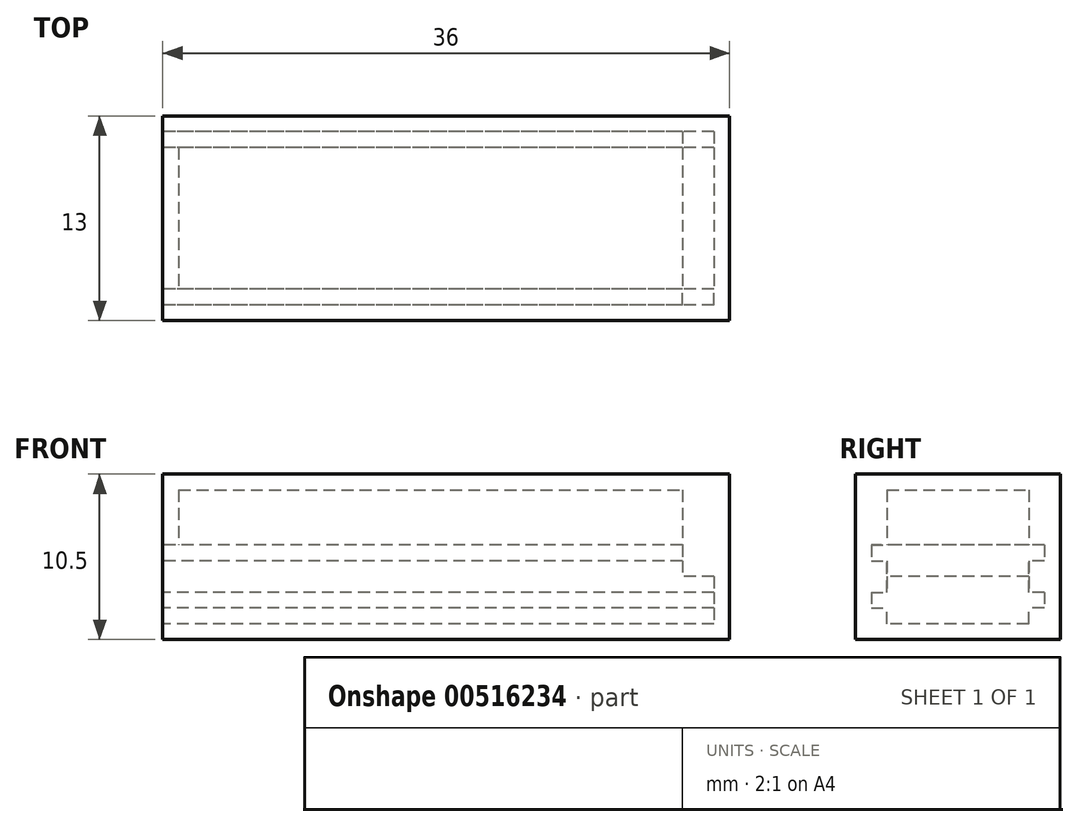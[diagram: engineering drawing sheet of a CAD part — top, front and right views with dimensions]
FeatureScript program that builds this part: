
annotation { "Feature Type Name" : "Feature", "Feature Type Description" : "" }
export const myFeature = defineFeature(function(context is Context, id is Id, definition is map)
    precondition{}
    {
        {
            var Q0;
            Q0=qCreatedBy(makeId("Top.planeOp"),FACE);
            var sketch = newSketch(context, id + "F0", { "sketchPlane" : qUnion([Q0])});
            skLineSegment(sketch, "E0.bottom", {"start": v(-27.77, -4.5) * mm, "end": v(4.23, -4.5) * mm});
            skLineSegment(sketch, "E0.top", {"start": v(-27.77, 4.5) * mm, "end": v(4.23, 4.5) * mm});
            skLineSegment(sketch, "E0.left", {"start": v(-27.77, -4.5) * mm, "end": v(-27.77, 4.5) * mm});
            skLineSegment(sketch, "E0.right", {"start": v(4.23, -4.5) * mm, "end": v(4.23, 4.5) * mm});
            skLineSegment(sketch, "E1.bottom", {"start": v(-28.77, -6.5) * mm, "end": v(7.23, -6.5) * mm});
            skLineSegment(sketch, "E1.top", {"start": v(-28.77, 6.5) * mm, "end": v(7.23, 6.5) * mm});
            skLineSegment(sketch, "E1.left", {"start": v(-28.77, -6.5) * mm, "end": v(-28.77, 6.5) * mm});
            skLineSegment(sketch, "E1.right", {"start": v(7.23, -6.5) * mm, "end": v(7.23, 6.5) * mm});
            skLineSegment(sketch, "E2", {"start": v(-28.77, 0) * mm, "end": v(7.23, 0) * mm, "construction": true});
            skLineSegment(sketch, "E3", {"start": v(-27.77, -4.5) * mm, "end": v(-28.77, -4.5) * mm});
            skLineSegment(sketch, "E4", {"start": v(-27.77, 4.5) * mm, "end": v(-28.77, 4.5) * mm});
            skSolve(sketch);
        }
        {
            var Q0;
            Q0=makeQuery(id+"F0.imprint","IMPRINT",FACE,{"disambiguationData":[TD([[makeQuery(id+"F0.imprint","IMPRINT",EDGE,{"derivedFrom":sQuery(id+"F0.wireOp",EDGE,"E0.bottom")}),-1.0]])]});
            var Q1;
            Q1=makeQuery(id+"F0.imprint","IMPRINT",FACE,{"disambiguationData":[TD([[makeQuery(id+"F0.imprint","IMPRINT",EDGE,{"derivedFrom":sQuery(id+"F0.wireOp",EDGE,"E0.bottom")}),1.0]])]});
            var Q2;
            Q2=makeQuery(id+"F0.imprint","IMPRINT",FACE,{"disambiguationData":[TD([[makeQuery(id+"F0.imprint","IMPRINT",EDGE,{"derivedFrom":sQuery(id+"F0.wireOp",EDGE,"E0.left")}),1.0]])]});
            extrude(context, id + "F1", {"entities" : qUnion([Q0, Q1, Q2]), "depth" : 6.5 * mm, "offsetDistance" : 25 * mm});
        }
        {
            var Q0;
            Q0=makeQuery(id+"F0.imprint","IMPRINT",FACE,{"disambiguationData":[TD([[makeQuery(id+"F0.imprint","IMPRINT",EDGE,{"derivedFrom":sQuery(id+"F0.wireOp",EDGE,"E0.bottom")}),1.0]])]});
            extrude(context, id + "F2", {"entities" : qUnion([Q0]), "operationType" : NewBodyOperationType.REMOVE, "depth" : 5.5 * mm, "offsetDistance" : 25 * mm});
        }
        {
            var Q0;
            Q0=makeQuery(id+"F0.imprint","IMPRINT",FACE,{"disambiguationData":[TD([[makeQuery(id+"F0.imprint","IMPRINT",EDGE,{"derivedFrom":sQuery(id+"F0.wireOp",EDGE,"E0.bottom")}),-1.0]])]});
            extrude(context, id + "F3", {"entities" : qUnion([Q0]), "operationType" : NewBodyOperationType.ADD, "oppositeDirection" : true, "depth" : 4 * mm, "offsetDistance" : 25 * mm});
        }
        {
            var Q0;
            {var subQ0=sQuery(id+"F0.wireOp",EDGE,"E1.left");Q0=makeQuery(id+"F3.boolean.opBoolean","MERGE",FACE,{"derivedFrom":[makeQuery(id+"F1.opExtrude","SWEPT_FACE",FACE,{"disambiguationData":[OSD([subQ0])]}),makeQuery(id+"F3.opExtrude","SWEPT_FACE",FACE,{"disambiguationData":[OSD([subQ0]),TDD([makeQuery(id+"F0.imprint","IMPRINT",EDGE,{"disambiguationData":[TD([[makeQuery(id+"F0.imprint","INTERSECT",VERTEX,{"derivedFrom":[sQuery(id+"F0.wireOp",EDGE,"E1.bottom"),subQ0]}),-1.0]])],"derivedFrom":subQ0})])]}),makeQuery(id+"F3.opExtrude","SWEPT_FACE",FACE,{"disambiguationData":[OSD([subQ0]),TDD([makeQuery(id+"F0.imprint","IMPRINT",EDGE,{"disambiguationData":[TD([[makeQuery(id+"F0.imprint","INTERSECT",VERTEX,{"derivedFrom":[sQuery(id+"F0.wireOp",EDGE,"E1.top"),subQ0]}),1.0]])],"derivedFrom":subQ0})])]})]});}
            var sketch = newSketch(context, id + "F4", { "sketchPlane" : qUnion([Q0])});
            skLineSegment(sketch, "E5.bottom", {"start": v(-5.5, -1) * mm, "end": v(-4.5, -1) * mm});
            skLineSegment(sketch, "E5.top", {"start": v(-5.5, -2) * mm, "end": v(-4.5, -2) * mm});
            skLineSegment(sketch, "E5.left", {"start": v(-5.5, -1) * mm, "end": v(-5.5, -2) * mm});
            skLineSegment(sketch, "E5.right", {"start": v(-4.5, -1) * mm, "end": v(-4.5, -2) * mm});
            skLineSegment(sketch, "E6", {"start": v(0, 0) * mm, "end": v(0, -9.1) * mm, "construction": true});
            skPoint(sketch, "E6.endSnap0", {"position": v(0, 0) * mm});
            skLineSegment(sketch, "E7.bottom", {"start": v(-4.5, -3) * mm, "end": v(4.5, -3) * mm});
            skLineSegment(sketch, "E7.top", {"start": v(-4.5, -4) * mm, "end": v(4.5, -4) * mm});
            skLineSegment(sketch, "E7.left", {"start": v(-4.5, -3) * mm, "end": v(-4.5, -4) * mm});
            skLineSegment(sketch, "E7.right", {"start": v(4.5, -3) * mm, "end": v(4.5, -4) * mm});
            skLineSegment(sketch, "E8.bottom", {"start": v(-5.5, 2) * mm, "end": v(-4.5, 2) * mm});
            skLineSegment(sketch, "E8.top", {"start": v(-5.5, 1) * mm, "end": v(-4.5, 1) * mm});
            skLineSegment(sketch, "E8.left", {"start": v(-5.5, 2) * mm, "end": v(-5.5, 1) * mm});
            skLineSegment(sketch, "E8.right", {"start": v(-4.5, 2) * mm, "end": v(-4.5, 1) * mm});
            skLineSegment(sketch, "E9.bottom", {"start": v(-4.5, 2) * mm, "end": v(0, 2) * mm});
            skLineSegment(sketch, "E9.top", {"start": v(-4.5, 0) * mm, "end": v(0, 0) * mm});
            skLineSegment(sketch, "E9.left", {"start": v(-4.5, 2) * mm, "end": v(-4.5, 0) * mm});
            skLineSegment(sketch, "E9.right", {"start": v(0, 2) * mm, "end": v(0, 0) * mm});
            skSolve(sketch);
        }
        {
            var Q0;
            Q0=makeQuery(id+"F4.imprint","IMPRINT",FACE,{"disambiguationData":[TD([[makeQuery(id+"F4.imprint","IMPRINT",EDGE,{"derivedFrom":sQuery(id+"F4.wireOp",EDGE,"E5.bottom")}),-1.0]])]});
            extrude(context, id + "F5", {"entities" : qUnion([Q0]), "operationType" : NewBodyOperationType.REMOVE, "oppositeDirection" : true, "depth" : 35 * mm, "offsetDistance" : 25 * mm});
        }
        {
            var Q0;
            Q0=makeQuery(id+"F4.imprint","IMPRINT",FACE,{"disambiguationData":[TD([[makeQuery(id+"F4.imprint","IMPRINT",EDGE,{"derivedFrom":sQuery(id+"F4.wireOp",EDGE,"E8.bottom")}),-1.0]])]});
            var Q1;
            {var subQ3=sQuery(id+"F4.wireOp",EDGE,"E9.bottom");Q1=makeQuery(id+"F4.imprint","IMPRINT",FACE,{"disambiguationData":[TD([[makeQuery(id+"F4.imprint","IMPRINT",EDGE,{"derivedFrom":subQ3}),-1.0]])]});}
            extrude(context, id + "F6", {"entities" : qUnion([Q0, Q1]), "operationType" : NewBodyOperationType.REMOVE, "oppositeDirection" : true, "depth" : 33 * mm, "offsetDistance" : 25 * mm});
        }
        {
            var Q0;
            Q0=makeQuery(id+"F1.opExtrude","SWEPT_BODY",BODY,{"disambiguationData":[OSD([sQuery(id+"F0.wireOp",EDGE,"E1.bottom"),sQuery(id+"F0.wireOp",EDGE,"E1.top"),sQuery(id+"F0.wireOp",EDGE,"E1.left"),sQuery(id+"F0.wireOp",EDGE,"E1.right")])]});
            var Q1;
            Q1=qCreatedBy(makeId("Front.planeOp"),FACE);
            mirror(context, id + "F7", {"operationType" : NewBodyOperationType.INTERSECT, "entities" : qUnion([Q0]), "mirrorPlane" : qUnion([Q1])});
        }
        {
            var Q0;
            {var subQ0=sQuery(id+"F0.wireOp",EDGE,"E0.right");Q0=makeQuery(id+"F3.boolean.opBoolean","MERGE",FACE,{"derivedFrom":[makeQuery(id+"F2.boolean.opBoolean","COPY",FACE,{"derivedFrom":makeQuery(id+"F2.opExtrude","SWEPT_FACE",FACE,{"disambiguationData":[OSD([subQ0])]})}),makeQuery(id+"F3.opExtrude","SWEPT_FACE",FACE,{"disambiguationData":[OSD([subQ0])]})]});}
            var sketch = newSketch(context, id + "F8", { "sketchPlane" : qUnion([Q0])});
            skLineSegment(sketch, "E10.bottom", {"start": v(-4.5, 0) * mm, "end": v(4.5, 0) * mm});
            skLineSegment(sketch, "E10.top", {"start": v(-4.5, -3) * mm, "end": v(4.5, -3) * mm});
            skLineSegment(sketch, "E10.left", {"start": v(-4.5, 0) * mm, "end": v(-4.5, -3) * mm});
            skLineSegment(sketch, "E10.right", {"start": v(4.5, 0) * mm, "end": v(4.5, -3) * mm});
            skSolve(sketch);
        }
        {
            var Q0;
            {var subQ3=sQuery(id+"F8.wireOp",EDGE,"E10.bottom");Q0=makeQuery(id+"F8.imprint","IMPRINT",FACE,{"disambiguationData":[TD([[makeQuery(id+"F8.imprint","IMPRINT",EDGE,{"derivedFrom":subQ3}),-1.0]])]});}
            extrude(context, id + "F9", {"entities" : qUnion([Q0]), "operationType" : NewBodyOperationType.REMOVE, "oppositeDirection" : true, "depth" : 2 * mm, "offsetDistance" : 25 * mm});
        }
        {
            var Q0;
            Q0=makeQuery(id+"F4.imprint","IMPRINT",FACE,{"disambiguationData":[TD([[makeQuery(id+"F4.imprint","IMPRINT",EDGE,{"derivedFrom":sQuery(id+"F4.wireOp",EDGE,"E7.bottom")}),-1.0]])]});
            var Q1;
            Q1=makeQuery(id+"F1.opExtrude","SWEPT_BODY",BODY,{"disambiguationData":[OSD([sQuery(id+"F0.wireOp",EDGE,"E1.bottom"),sQuery(id+"F0.wireOp",EDGE,"E1.top"),sQuery(id+"F0.wireOp",EDGE,"E1.left"),sQuery(id+"F0.wireOp",EDGE,"E1.right")])]});
            extrude(context, id + "F10", {"entities" : qUnion([Q0]), "operationType" : NewBodyOperationType.ADD, "endBound" : BoundingType.UP_TO_BODY, "oppositeDirection" : true, "depth" : 25 * mm, "endBoundEntityBody" : qUnion([Q1]), "offsetDistance" : 25 * mm});
        }
    });
